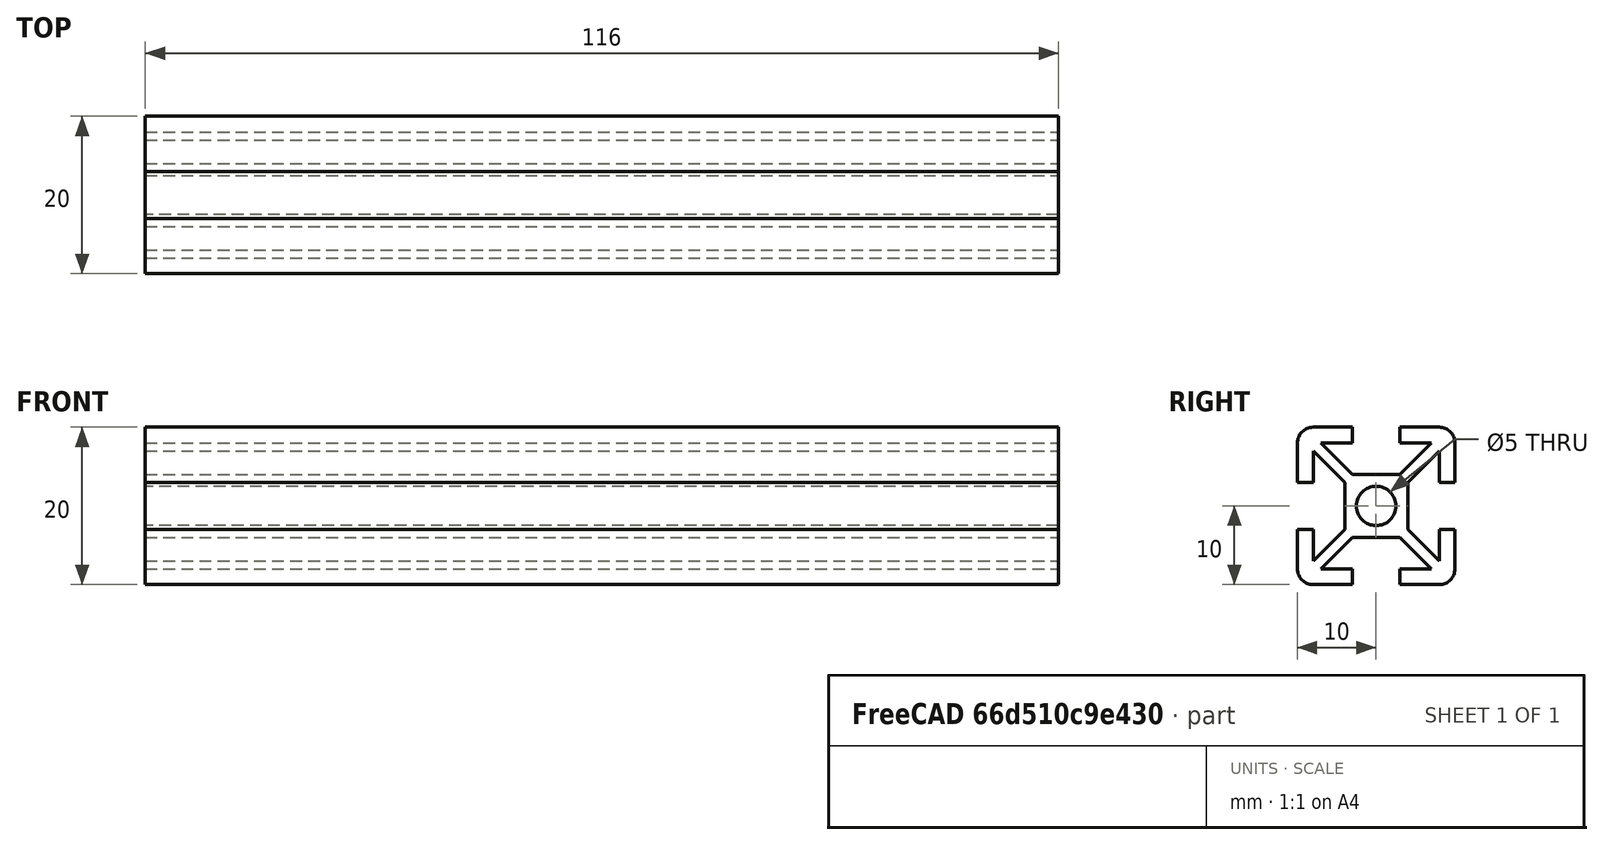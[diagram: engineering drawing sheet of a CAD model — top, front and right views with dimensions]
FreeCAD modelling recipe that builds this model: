
FCSTD DOCUMENT  (FreeCAD 0.19R24267 +99 (Git))
Label: 2020 Rail strut spacer front back 116mm
License: All rights reserved
LicenseURL: http://en.wikipedia.org/wiki/All_rights_reserved
objects: Sketcher::SketchObject×1, PartDesign::Pad×1, PartDesign::Body×1
note: 4 computed .brp shape members not serialized (recipe doc carries the construction recipe); baked Part::Feature solids carry a one-line shape summary decoded from their .brp

FEATURE [Sketcher::SketchObject] Sketch  label="Rail cross section"
  FullyConstrained = true
  MapMode = 5
  Placement = pos=(0,0,0) rot=(0.57735,0.57735,0.57735;2.0944rad)
  Support = -> [YZ_Plane]
  sketch-geometry (47):
    g0: ArcOfCircle CenterX=-8 CenterY=8 CenterZ=0 NormalX=0 NormalY=0 NormalZ=1 AngleXU=0 Radius=2 StartAngle=1.5708 EndAngle=3.14159
    g1: ArcOfCircle CenterX=-8 CenterY=-8 CenterZ=0 NormalX=0 NormalY=0 NormalZ=1 AngleXU=0 Radius=2 StartAngle=3.14159 EndAngle=4.71239
    g2: ArcOfCircle CenterX=8 CenterY=-8 CenterZ=0 NormalX=0 NormalY=0 NormalZ=1 AngleXU=0 Radius=2 StartAngle=4.71239 EndAngle=6.28319
    g3: ArcOfCircle CenterX=8 CenterY=8 CenterZ=0 NormalX=0 NormalY=0 NormalZ=1 AngleXU=0 Radius=2 StartAngle=2e-16 EndAngle=1.5708
    g4: Circle CenterX=0 CenterY=0 CenterZ=0 NormalX=0 NormalY=0 NormalZ=1 AngleXU=0 Radius=2.5
    g5: LineSegment StartX=-10 StartY=8 StartZ=0 EndX=-10 EndY=3 EndZ=0
    g6: LineSegment StartX=-10 StartY=-3 StartZ=0 EndX=-10 EndY=-8 EndZ=0
    g7: LineSegment StartX=-8 StartY=-10 StartZ=0 EndX=-3 EndY=-10 EndZ=0
    g8: LineSegment StartX=3 StartY=-10 StartZ=0 EndX=8 EndY=-10 EndZ=0
    g9: LineSegment StartX=10 StartY=-8 StartZ=0 EndX=10 EndY=-3 EndZ=0
    g10: LineSegment StartX=10 StartY=3 StartZ=0 EndX=10 EndY=8 EndZ=0
    g11: LineSegment StartX=-8 StartY=10 StartZ=0 EndX=-3 EndY=10 EndZ=0
    g12: LineSegment StartX=3 StartY=10 StartZ=0 EndX=8 EndY=10 EndZ=0
    g13: LineSegment StartX=-3 StartY=4 StartZ=0 EndX=3 EndY=4 EndZ=0
    g14: LineSegment StartX=4 StartY=3 StartZ=0 EndX=4 EndY=-3 EndZ=0
    g15: LineSegment StartX=3 StartY=-4 StartZ=0 EndX=-3 EndY=-4 EndZ=0
    g16: LineSegment StartX=-4 StartY=-3 StartZ=0 EndX=-4 EndY=3 EndZ=0
    g17: LineSegment StartX=-3 StartY=-4 StartZ=0 EndX=-7 EndY=-8 EndZ=0
    g18: LineSegment StartX=-3 StartY=-10 StartZ=0 EndX=-3 EndY=-8 EndZ=0
    g19: LineSegment StartX=3 StartY=-4 StartZ=0 EndX=7 EndY=-8 EndZ=0
    g20: LineSegment StartX=4 StartY=-3 StartZ=0 EndX=8 EndY=-7 EndZ=0
    g21: LineSegment StartX=8 StartY=-7 StartZ=0 EndX=8 EndY=-3 EndZ=0
    g22: LineSegment StartX=10 StartY=-3 StartZ=0 EndX=8 EndY=-3 EndZ=0
    g23: LineSegment StartX=4 StartY=3 StartZ=0 EndX=8 EndY=7 EndZ=0
    g24: LineSegment StartX=8 StartY=7 StartZ=0 EndX=8 EndY=3 EndZ=0
    g25: LineSegment StartX=8 StartY=3 StartZ=0 EndX=10 EndY=3 EndZ=0
    g26: LineSegment StartX=3 StartY=10 StartZ=0 EndX=3 EndY=8 EndZ=0
    g27: LineSegment StartX=3 StartY=8 StartZ=0 EndX=7 EndY=8 EndZ=0
    g28: LineSegment StartX=7 StartY=8 StartZ=0 EndX=3 EndY=4 EndZ=0
    g29: LineSegment StartX=-3 StartY=4 StartZ=0 EndX=-7 EndY=8 EndZ=0
    g30: LineSegment StartX=-7 StartY=8 StartZ=0 EndX=-3 EndY=8 EndZ=0
    g31: LineSegment StartX=-3 StartY=8 StartZ=0 EndX=-3 EndY=10 EndZ=0
    g32: LineSegment StartX=-4 StartY=3 StartZ=0 EndX=-8 EndY=7 EndZ=0
    g33: LineSegment StartX=-8 StartY=3 StartZ=0 EndX=-10 EndY=3 EndZ=0
    g34: LineSegment StartX=-10 StartY=-3 StartZ=0 EndX=-8 EndY=-3 EndZ=0
    g35: LineSegment StartX=-8 StartY=-7 StartZ=0 EndX=-4 EndY=-3 EndZ=0
    g36: LineSegment StartX=3 StartY=-10 StartZ=0 EndX=3 EndY=-8 EndZ=0
    g37: LineSegment StartX=3 StartY=-8 StartZ=0 EndX=7 EndY=-8 EndZ=0
    g38: LineSegment StartX=-3 StartY=-8 StartZ=0 EndX=-7 EndY=-8 EndZ=0
    g39: LineSegment StartX=-8 StartY=-7 StartZ=0 EndX=-8 EndY=-3 EndZ=0
    g40: LineSegment StartX=-8 StartY=3 StartZ=0 EndX=-8 EndY=7 EndZ=0
    g41: LineSegment StartX=-3 StartY=10 StartZ=0 EndX=3 EndY=10 EndZ=0
    g42: LineSegment StartX=10 StartY=3 StartZ=0 EndX=10 EndY=-3 EndZ=0
    g43: LineSegment StartX=3 StartY=-10 StartZ=0 EndX=-3 EndY=-10 EndZ=0
    g44: LineSegment StartX=-10 StartY=-3 StartZ=0 EndX=-10 EndY=3 EndZ=0
    g45: LineSegment StartX=-4 StartY=-3 StartZ=0 EndX=-3 EndY=-4 EndZ=0
    g46: LineSegment StartX=-8 StartY=-7 StartZ=0 EndX=-7 EndY=-8 EndZ=0
  constraints (128):
    c: Radius(g0) = 2  'ASSUMED EDGE RADIUS'
    c: Equal(g1,g2)
    c: Coincident(g4,g-1)
    c: Radius(g4) = 2.5  'CENTER HOLE'
    c: Vertical(g6)
    c: Horizontal(g7)
    c: Horizontal(g8)
    c: Vertical(g9)
    c: Vertical(g10)
    c: Horizontal(g11)
    c: Horizontal(g12)
    c: DistanceX(g0,g3) = 20  'RAIL WIDTH'
    c: Vertical(g5)
    c: DistanceY(g2,g3) = 20  'RAIL HEIGHT'
    c: DistanceX(g7,g8) = 6  'SLOT WIDTH'
    c: Equal(g8,g7)
    c: Equal(g7,g6)
    c: Equal(g5,g11)
    c: Equal(g12,g10)
    c: Tangent(g12,g3) = 1.5708
    c: Tangent(g10,g3) = -1.5708
    c: Tangent(g11,g0) = 1.5708
    c: Tangent(g5,g0) = -1.5708
    c: Tangent(g6,g1) = -1.5708
    c: Tangent(g7,g1) = -1.5708
    c: Tangent(g8,g2) = -1.5708
    c: Tangent(g9,g2) = -1.5708
    c: Symmetric(g3,g2,g-1)
    c: Symmetric(g0,g3,g-2)
    c: Horizontal(g13)
    c: Vertical(g14)
    c: Vertical(g16)
    c: Horizontal(g15)
    c: Equal(g16,g15)
    c: Equal(g15,g14)
    c: Coincident(g17,g15)
    c: Coincident(g18,g7)
    c: Vertical(g18)
    c: Coincident(g19,g15)
    c: Coincident(g20,g14)
    c: Coincident(g21,g20)
    c: Vertical(g21)
    c: Coincident(g22,g9)
    c: Coincident(g22,g21)
    c: Coincident(g23,g14)
    c: Coincident(g24,g23)
    c: Vertical(g24)
    c: Coincident(g25,g24)
    c: Coincident(g25,g10)
    c: Coincident(g26,g12)
    c: Vertical(g26)
    c: Coincident(g27,g26)
    c: Horizontal(g27)
    c: Coincident(g28,g27)
    c: Coincident(g28,g13)
    c: Coincident(g29,g13)
    c: Coincident(g30,g29)
    c: Horizontal(g30)
    c: Coincident(g31,g30)
    c: Coincident(g31,g11)
    c: Coincident(g32,g16)
    c: Coincident(g33,g5)
    c: Horizontal(g33)
    c: Coincident(g34,g6)
    c: Horizontal(g34)
    c: Coincident(g35,g16)
    c: Coincident(g36,g8)
    c: Vertical(g36)
    c: Coincident(g37,g36)
    c: Coincident(g37,g19)
    c: Coincident(g38,g18)
    c: Coincident(g38,g17)
    c: Horizontal(g38)
    c: Coincident(g39,g35)
    c: Coincident(g39,g34)
    c: Vertical(g39)
    c: Coincident(g40,g33)
    c: Coincident(g40,g32)
    c: Vertical(g40)
    c: Horizontal(g37)
    c: Horizontal(g25)
    c: Horizontal(g22)
    c: Equal(g38,g37)
    c: Equal(g37,g21)
    c: Equal(g21,g24)
    c: Equal(g24,g27)
    c: Equal(g27,g30)
    c: Equal(g30,g40)
    c: Equal(g40,g39)
    c: Vertical(g31)
    c: Equal(g31,g26)
    c: Equal(g26,g25)
    c: Equal(g25,g22)
    c: Equal(g22,g36)
    c: Equal(g36,g18)
    c: Equal(g18,g34)
    c: Equal(g34,g33)
    c: Equal(g32,g29)
    c: Equal(g29,g28)
    c: Equal(g28,g23)
    c: Equal(g23,g20)
    c: Equal(g20,g19)
    c: Equal(g19,g17)
    c: Equal(g17,g35)
    c: Coincident(g41,g11)
    c: Coincident(g41,g12)
    c: Coincident(g42,g10)
    c: Coincident(g42,g9)
    c: Coincident(g43,g8)
    c: Coincident(g43,g7)
    c: Horizontal(g43)
    c: Coincident(g44,g6)
    c: Coincident(g44,g5)
    c: Vertical(g44)
    c: Horizontal(g41)
    c: DistanceY(g8,g15) = 6  'ASSUMED SLOT DEPTH'
    c: Equal(g43,g15)
    c: Equal(g16,g13)
    c: Equal(g44,g43)
    c: Equal(g43,g42)
    c: Equal(g42,g41)
    c: Vertical(g42)
    c: DistanceY(g36,g36) = 2  'ASSUMED WALL THICKNESS'
    c: Coincident(g45,g16)
    c: Coincident(g45,g15)
    c: Coincident(g46,g35)
    c: Coincident(g46,g17)
    c: Equal(g45,g46)
FEATURE [PartDesign::Pad] Pad  label="Length"
  Direction = (1,1,1)
  Length = 116
  Length2 = 100
  Placement = pos=(0,0,0) rot=(0.57735,0.57735,0.57735;2.0944rad)
  Profile = -> Sketch
  Type = 0
FEATURE [PartDesign::Body] Body
  Group = -> [Sketch,Pad]
  Origin = -> Origin
  Tip = -> Pad
